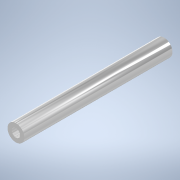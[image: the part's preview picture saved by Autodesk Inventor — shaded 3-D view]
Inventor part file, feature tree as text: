
AUTODESK INVENTOR PART (.ipt)
format: ipt  version: 2020.3 (Build 243373000, 373)  size: 100,352 bytes
history: native  units: mm
features: other x1, extrude x1, sketch x1
ambient origin geometry x8: Origin, YZ Plane, XZ Plane, XY Plane, X Axis, Y Axis, Z Axis, Center Point
bodies: Body1 (feature_tree)
feature tree (3):
  other  "ソリッド1"
  extrude  "押し出し1"  Depth=6.0mm
  sketch  "スケッチ1"
